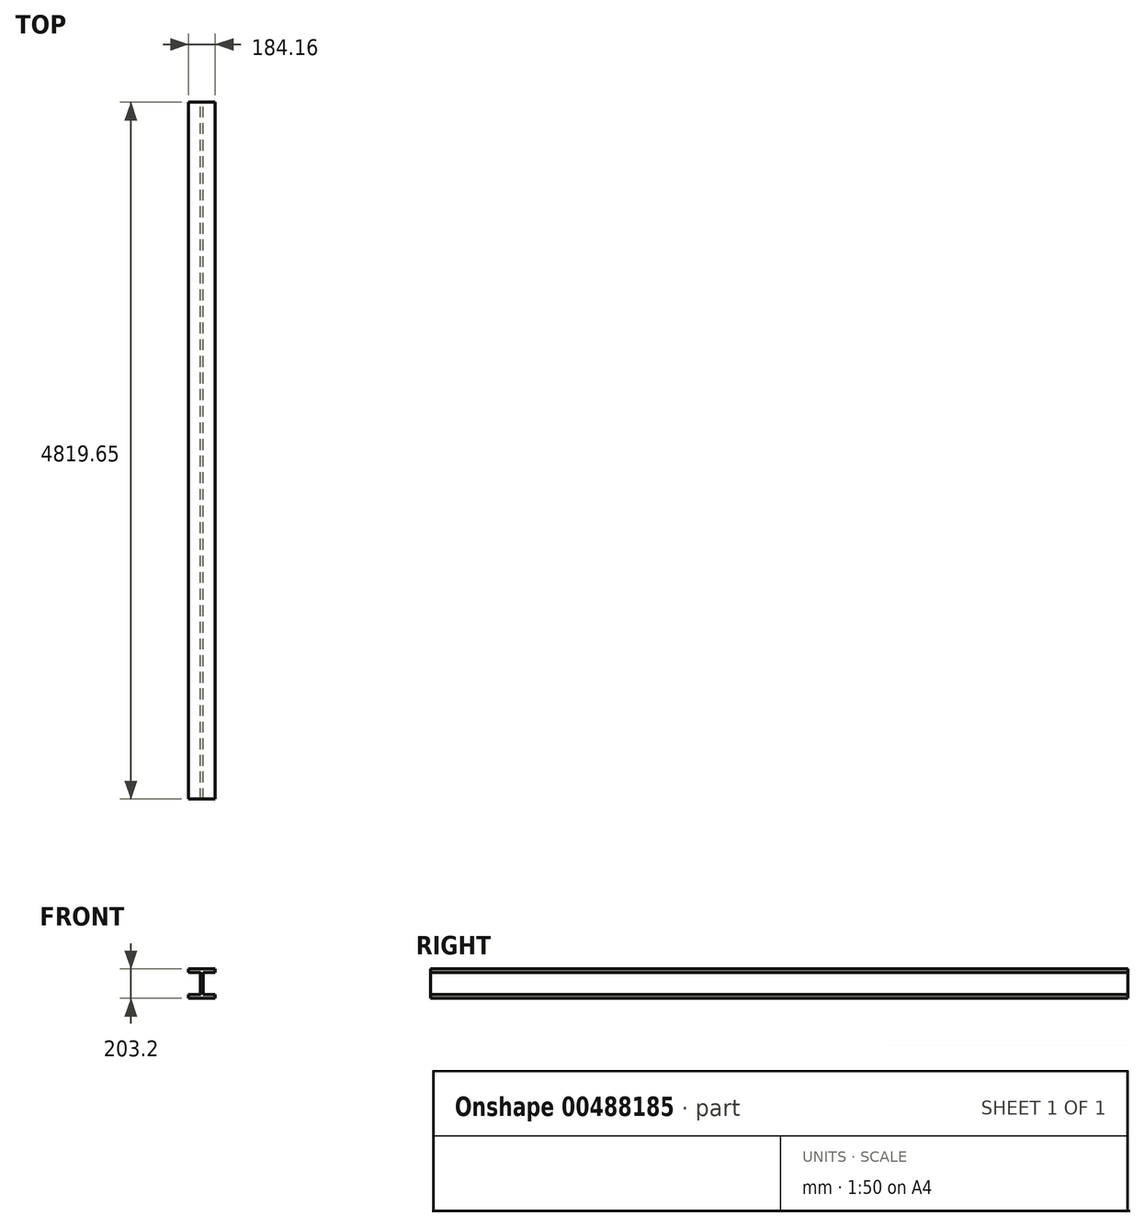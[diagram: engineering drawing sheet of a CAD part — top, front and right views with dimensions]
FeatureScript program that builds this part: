
annotation { "Feature Type Name" : "Feature", "Feature Type Description" : "" }
export const myFeature = defineFeature(function(context is Context, id is Id, definition is map)
    precondition{}
    {
        {
            var Q0;
            Q0=qCreatedBy(makeId("Front.planeOp"),FACE);
            var sketch = newSketch(context, id + "F0", { "sketchPlane" : qUnion([Q0])});
            skLineSegment(sketch, "E0", {"start": v(92.08, -76.2) * mm, "end": v(12.07, -76.2) * mm});
            skLineSegment(sketch, "E1", {"start": v(9.52, -73.66) * mm, "end": v(9.52, 73.66) * mm});
            skLineSegment(sketch, "E2", {"start": v(12.07, 76.2) * mm, "end": v(92.08, 76.2) * mm});
            skLineSegment(sketch, "E3", {"start": v(-92.08, 76.2) * mm, "end": v(-12.07, 76.2) * mm});
            skLineSegment(sketch, "E4", {"start": v(-9.53, 73.66) * mm, "end": v(-9.53, -73.66) * mm});
            skLineSegment(sketch, "E5", {"start": v(-12.06, -76.2) * mm, "end": v(-92.08, -76.2) * mm});
            skLineSegment(sketch, "E6", {"start": v(0, 0) * mm, "end": v(-9.52, 0) * mm, "construction": true});
            skLineSegment(sketch, "E7", {"start": v(0, 0) * mm, "end": v(9.52, 0) * mm, "construction": true});
            skLineSegment(sketch, "E8", {"start": v(0, 0) * mm, "end": v(0, 101.6) * mm, "construction": true});
            skLineSegment(sketch, "E9", {"start": v(0, 0) * mm, "end": v(0, -101.6) * mm, "construction": true});
            skPoint(sketch, "E10.visualSharp", {"position": v(-9.53, 76.2) * mm});
            skArc(sketch, "E10.filletArc", {"start": v(-9.52, 73.66) * mm, "mid": v(-10.27, 75.46) * mm, "end": v(-12.07, 76.2) * mm});
            skPoint(sketch, "E11.visualSharp", {"position": v(9.53, 76.2) * mm});
            skArc(sketch, "E11.filletArc", {"start": v(12.07, 76.2) * mm, "mid": v(10.27, 75.46) * mm, "end": v(9.52, 73.66) * mm});
            skPoint(sketch, "E12.visualSharp", {"position": v(9.53, -76.2) * mm});
            skArc(sketch, "E12.filletArc", {"start": v(9.52, -73.66) * mm, "mid": v(10.27, -75.46) * mm, "end": v(12.07, -76.2) * mm});
            skPoint(sketch, "E13.visualSharp", {"position": v(-9.53, -76.2) * mm});
            skArc(sketch, "E13.filletArc", {"start": v(-12.06, -76.2) * mm, "mid": v(-10.27, -75.46) * mm, "end": v(-9.52, -73.66) * mm});
            skPoint(sketch, "E14.visualSharp", {"position": v(-92.08, 101.6) * mm});
            skPoint(sketch, "E15.visualSharp", {"position": v(92.08, 101.6) * mm});
            skPoint(sketch, "E16.visualSharp", {"position": v(92.08, 76.2) * mm});
            skPoint(sketch, "E17.visualSharp", {"position": v(92.08, -101.6) * mm});
            skPoint(sketch, "E18.visualSharp", {"position": v(-92.08, -76.2) * mm});
            skPoint(sketch, "E19.visualSharp", {"position": v(-92.08, -101.6) * mm});
            skLineSegment(sketch, "E20", {"start": v(92.08, -76.2) * mm, "end": v(92.08, -101.6) * mm});
            skLineSegment(sketch, "E21", {"start": v(-92.08, -76.2) * mm, "end": v(-92.08, -101.6) * mm});
            skLineSegment(sketch, "E22", {"start": v(-92.08, 101.6) * mm, "end": v(-92.08, 76.2) * mm});
            skLineSegment(sketch, "E23", {"start": v(92.08, 101.6) * mm, "end": v(92.08, 76.2) * mm});
            skLineSegment(sketch, "E24", {"start": v(-92.08, 101.6) * mm, "end": v(92.08, 101.6) * mm});
            skLineSegment(sketch, "E25", {"start": v(-92.07, -101.6) * mm, "end": v(92.08, -101.6) * mm});
            skSolve(sketch);
        }
        {
            var Q0;
            Q0=makeQuery(id+"F0.imprint","IMPRINT",FACE,{"disambiguationData":[TD([[makeQuery(id+"F0.imprint","IMPRINT",EDGE,{"derivedFrom":sQuery(id+"F0.wireOp",EDGE,"E0")}),1.0]])]});
            extrude(context, id + "F1", {"entities" : qUnion([Q0]), "depth" : 4572 * mm + 247.65 * mm, "offsetDistance" : 25.4 * mm});
        }
    });
